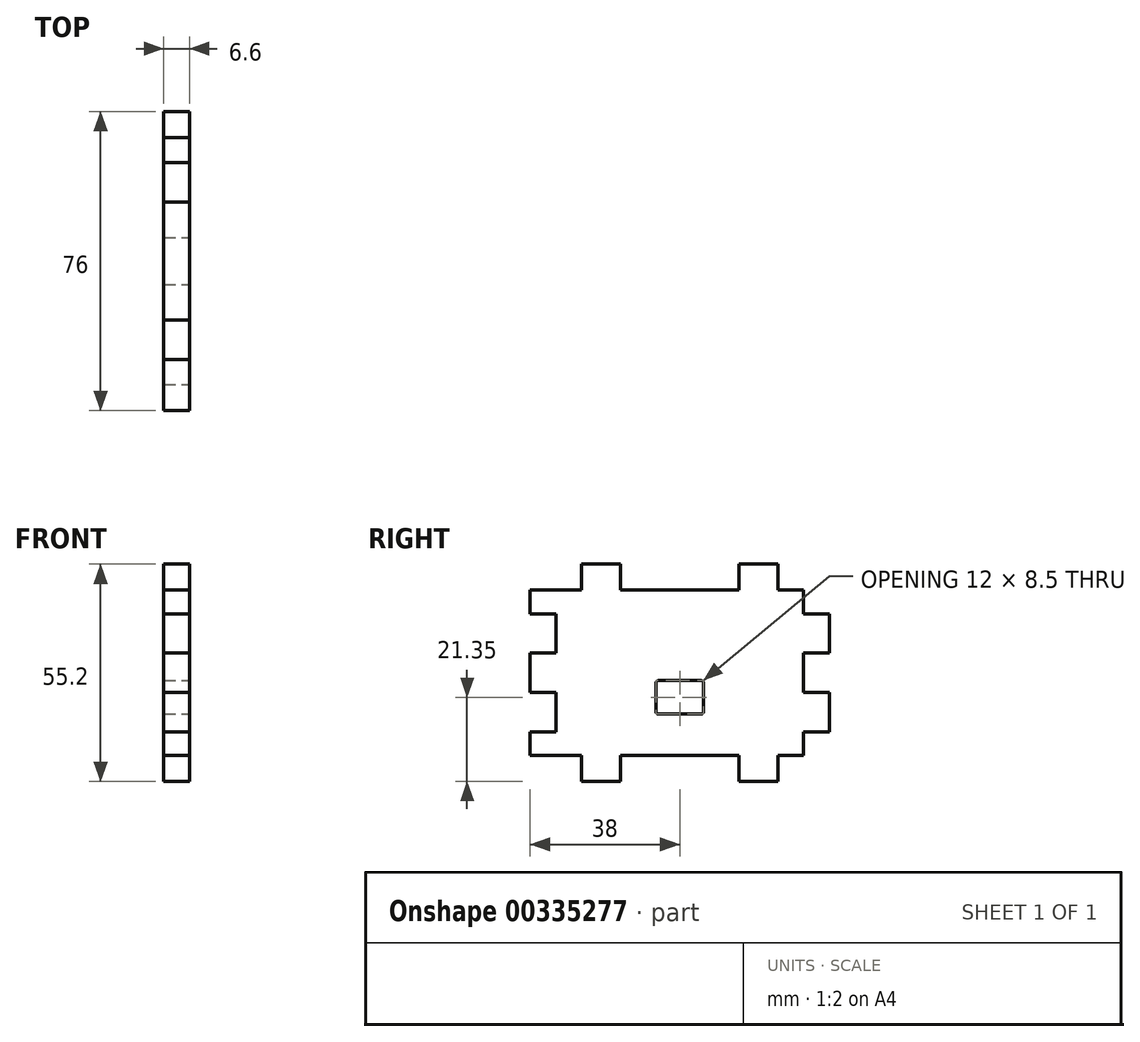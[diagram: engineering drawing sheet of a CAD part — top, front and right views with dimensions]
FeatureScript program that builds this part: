
annotation { "Feature Type Name" : "Feature", "Feature Type Description" : "" }
export const myFeature = defineFeature(function(context is Context, id is Id, definition is map)
    precondition{}
    {
        {
            var Q0;
            Q0=qCreatedBy(makeId("Right.planeOp"),FACE);
            var sketch = newSketch(context, id + "F0", { "sketchPlane" : qUnion([Q0])});
            skLineSegment(sketch, "E0.bottom", {"start": v(38, 21) * mm, "end": v(-38, 21) * mm});
            skLineSegment(sketch, "E0.top", {"start": v(38, -21) * mm, "end": v(-38, -21) * mm});
            skLineSegment(sketch, "E0.left", {"start": v(38, 21) * mm, "end": v(38, -21) * mm});
            skLineSegment(sketch, "E0.right", {"start": v(-38, 21) * mm, "end": v(-38, -21) * mm});
            skPoint(sketch, "E0.middle", {"position": v(0, 0) * mm});
            skSolve(sketch);
        }
        {
            var Q0;
            Q0=qSketchRegion(id+"F0",true);
            extrude(context, id + "F1", {"entities" : qUnion([Q0]), "depth" : 6.6 * mm});
        }
        {
            var Q0;
            Q0=makeQuery(id+"F1.opExtrude","CAP_FACE",FACE,{"disambiguationData":[OSD([sQuery(id+"F0.wireOp",EDGE,"E0.bottom"),sQuery(id+"F0.wireOp",EDGE,"E0.top"),sQuery(id+"F0.wireOp",EDGE,"E0.left"),sQuery(id+"F0.wireOp",EDGE,"E0.right")])],"isStart":false});
            var sketch = newSketch(context, id + "F2", { "sketchPlane" : qUnion([Q0])});
            skLineSegment(sketch, "E1", {"start": v(0, 21) * mm, "end": v(0, -21) * mm, "construction": true});
            skLineSegment(sketch, "E2", {"start": v(-38, 0) * mm, "end": v(38, 0) * mm, "construction": true});
            skLineSegment(sketch, "E3.bottom", {"start": v(-25, 27.6) * mm, "end": v(-15, 27.6) * mm});
            skLineSegment(sketch, "E3.top", {"start": v(-25, 21) * mm, "end": v(-15, 21) * mm});
            skLineSegment(sketch, "E3.left", {"start": v(-25, 27.6) * mm, "end": v(-25, 21) * mm});
            skLineSegment(sketch, "E3.right", {"start": v(-15, 27.6) * mm, "end": v(-15, 21) * mm});
            skLineSegment(sketch, "E4.MirrorCS", {"start": v(15, 27.6) * mm, "end": v(15, 21) * mm});
            skLineSegment(sketch, "E5.MirrorCS", {"start": v(25, 27.6) * mm, "end": v(25, 21) * mm});
            skLineSegment(sketch, "E6.MirrorCS", {"start": v(25, 21) * mm, "end": v(15, 21) * mm});
            skLineSegment(sketch, "E7.MirrorCS", {"start": v(25, 27.6) * mm, "end": v(15, 27.6) * mm});
            skLineSegment(sketch, "E8.MirrorCS", {"start": v(15, -27.6) * mm, "end": v(15, -21) * mm});
            skLineSegment(sketch, "E9.MirrorCS", {"start": v(-15, -27.6) * mm, "end": v(-15, -21) * mm});
            skLineSegment(sketch, "E10.MirrorCS", {"start": v(-25, -27.6) * mm, "end": v(-25, -21) * mm});
            skLineSegment(sketch, "E11.MirrorCS", {"start": v(-25, -21) * mm, "end": v(-15, -21) * mm});
            skLineSegment(sketch, "E12.MirrorCS", {"start": v(-25, -27.6) * mm, "end": v(-15, -27.6) * mm});
            skLineSegment(sketch, "E13.MirrorCS", {"start": v(25, -27.6) * mm, "end": v(25, -21) * mm});
            skLineSegment(sketch, "E14.MirrorCS", {"start": v(25, -21) * mm, "end": v(15, -21) * mm});
            skLineSegment(sketch, "E15.MirrorCS", {"start": v(25, -27.6) * mm, "end": v(15, -27.6) * mm});
            skSolve(sketch);
        }
        {
            var Q0;
            Q0 = qSketchRegion(id + "F2", true);
            extrude(context, id + "F3", {"entities" : qUnion([Q0]), "operationType" : NewBodyOperationType.ADD, "oppositeDirection" : true, "depth" : 6.6 * mm});
        }
        {
            var Q0;
            Q0=makeQuery(id+"F3.boolean.opBoolean","MERGE",FACE,{"derivedFrom":[makeQuery(id+"F1.opExtrude","CAP_FACE",FACE,{"disambiguationData":[OSD([sQuery(id+"F0.wireOp",EDGE,"E0.bottom"),sQuery(id+"F0.wireOp",EDGE,"E0.top"),sQuery(id+"F0.wireOp",EDGE,"E0.left"),sQuery(id+"F0.wireOp",EDGE,"E0.right")])],"isStart":false}),makeQuery(id+"F3.opExtrude","CAP_FACE",FACE,{"disambiguationData":[OSD([sQuery(id+"F2.wireOp",EDGE,"E3.bottom"),sQuery(id+"F2.wireOp",EDGE,"E3.top"),sQuery(id+"F2.wireOp",EDGE,"E3.left"),sQuery(id+"F2.wireOp",EDGE,"E3.right")])],"isStart":true}),makeQuery(id+"F3.opExtrude","CAP_FACE",FACE,{"disambiguationData":[OSD([sQuery(id+"F2.wireOp",EDGE,"E4.MirrorCS"),sQuery(id+"F2.wireOp",EDGE,"E5.MirrorCS"),sQuery(id+"F2.wireOp",EDGE,"E6.MirrorCS"),sQuery(id+"F2.wireOp",EDGE,"E7.MirrorCS")])],"isStart":true}),makeQuery(id+"F3.opExtrude","CAP_FACE",FACE,{"disambiguationData":[OSD([sQuery(id+"F2.wireOp",EDGE,"E8.MirrorCS"),sQuery(id+"F2.wireOp",EDGE,"E13.MirrorCS"),sQuery(id+"F2.wireOp",EDGE,"E14.MirrorCS"),sQuery(id+"F2.wireOp",EDGE,"E15.MirrorCS")])],"isStart":true}),makeQuery(id+"F3.opExtrude","CAP_FACE",FACE,{"disambiguationData":[OSD([sQuery(id+"F2.wireOp",EDGE,"E9.MirrorCS"),sQuery(id+"F2.wireOp",EDGE,"E10.MirrorCS"),sQuery(id+"F2.wireOp",EDGE,"E11.MirrorCS"),sQuery(id+"F2.wireOp",EDGE,"E12.MirrorCS")])],"isStart":true})]});
            var sketch = newSketch(context, id + "F4", { "sketchPlane" : qUnion([Q0])});
            skLineSegment(sketch, "E16", {"start": v(31.4, 21) * mm, "end": v(31.4, -21) * mm, "construction": true});
            skPoint(sketch, "E16.endSnap0", {"position": v(31.5, -21) * mm});
            skLineSegment(sketch, "E17.bottom", {"start": v(31.4, 21) * mm, "end": v(38, 21) * mm});
            skLineSegment(sketch, "E17.top", {"start": v(31.4, 15) * mm, "end": v(38, 15) * mm});
            skLineSegment(sketch, "E17.left", {"start": v(31.4, 21) * mm, "end": v(31.4, 15) * mm});
            skLineSegment(sketch, "E17.right", {"start": v(38, 21) * mm, "end": v(38, 15) * mm});
            skLineSegment(sketch, "E18", {"start": v(-38, 0) * mm, "end": v(38, 0) * mm, "construction": true});
            skLineSegment(sketch, "E19.MirrorCS", {"start": v(31.4, -15) * mm, "end": v(38, -15) * mm});
            skLineSegment(sketch, "E20.MirrorCS", {"start": v(31.4, -21) * mm, "end": v(31.4, -15) * mm});
            skLineSegment(sketch, "E21.MirrorCS", {"start": v(31.4, -21) * mm, "end": v(38, -21) * mm});
            skLineSegment(sketch, "E22.MirrorCS", {"start": v(38, -21) * mm, "end": v(38, -15) * mm});
            skLineSegment(sketch, "E23.bottom", {"start": v(31.4, 5) * mm, "end": v(38, 5) * mm});
            skLineSegment(sketch, "E23.top", {"start": v(31.4, -5) * mm, "end": v(38, -5) * mm});
            skLineSegment(sketch, "E23.left", {"start": v(31.4, 5) * mm, "end": v(31.4, -5) * mm});
            skLineSegment(sketch, "E23.right", {"start": v(38, 5) * mm, "end": v(38, -5) * mm});
            skPoint(sketch, "E23.middle", {"position": v(34.7, 0) * mm});
            skLineSegment(sketch, "E24", {"start": v(0, 21) * mm, "end": v(0, -21) * mm, "construction": true});
            skLineSegment(sketch, "E25.MirrorCS", {"start": v(-31.4, 21) * mm, "end": v(-31.4, -21) * mm, "construction": true});
            skLineSegment(sketch, "E26.bottom", {"start": v(-38, 15) * mm, "end": v(-31.4, 15) * mm});
            skLineSegment(sketch, "E26.top", {"start": v(-38, 5) * mm, "end": v(-31.4, 5) * mm});
            skLineSegment(sketch, "E26.left", {"start": v(-38, 15) * mm, "end": v(-38, 5) * mm});
            skLineSegment(sketch, "E26.right", {"start": v(-31.4, 15) * mm, "end": v(-31.4, 5) * mm});
            skLineSegment(sketch, "E27.MirrorCS", {"start": v(-38, -5) * mm, "end": v(-31.4, -5) * mm});
            skLineSegment(sketch, "E28.MirrorCS", {"start": v(-31.4, -15) * mm, "end": v(-31.4, -5) * mm});
            skLineSegment(sketch, "E29.MirrorCS", {"start": v(-38, -15) * mm, "end": v(-31.4, -15) * mm});
            skLineSegment(sketch, "E30.MirrorCS", {"start": v(-38, -15) * mm, "end": v(-38, -5) * mm});
            skSolve(sketch);
        }
        {
            var Q0;
            Q0 = qSketchRegion(id + "F4", true);
            extrude(context, id + "F5", {"entities" : qUnion([Q0]), "operationType" : NewBodyOperationType.REMOVE, "endBound" : BoundingType.UP_TO_NEXT, "oppositeDirection" : true, "depth" : 25 * mm});
        }
        {
            var Q0;
            Q0=makeQuery(id+"F3.boolean.opBoolean","MERGE",FACE,{"derivedFrom":[makeQuery(id+"F1.opExtrude","CAP_FACE",FACE,{"disambiguationData":[OSD([sQuery(id+"F0.wireOp",EDGE,"E0.bottom"),sQuery(id+"F0.wireOp",EDGE,"E0.top"),sQuery(id+"F0.wireOp",EDGE,"E0.left"),sQuery(id+"F0.wireOp",EDGE,"E0.right")])],"isStart":false}),makeQuery(id+"F3.opExtrude","CAP_FACE",FACE,{"disambiguationData":[OSD([sQuery(id+"F2.wireOp",EDGE,"E3.bottom"),sQuery(id+"F2.wireOp",EDGE,"E3.top"),sQuery(id+"F2.wireOp",EDGE,"E3.left"),sQuery(id+"F2.wireOp",EDGE,"E3.right")])],"isStart":true}),makeQuery(id+"F3.opExtrude","CAP_FACE",FACE,{"disambiguationData":[OSD([sQuery(id+"F2.wireOp",EDGE,"E4.MirrorCS"),sQuery(id+"F2.wireOp",EDGE,"E5.MirrorCS"),sQuery(id+"F2.wireOp",EDGE,"E6.MirrorCS"),sQuery(id+"F2.wireOp",EDGE,"E7.MirrorCS")])],"isStart":true}),makeQuery(id+"F3.opExtrude","CAP_FACE",FACE,{"disambiguationData":[OSD([sQuery(id+"F2.wireOp",EDGE,"E8.MirrorCS"),sQuery(id+"F2.wireOp",EDGE,"E13.MirrorCS"),sQuery(id+"F2.wireOp",EDGE,"E14.MirrorCS"),sQuery(id+"F2.wireOp",EDGE,"E15.MirrorCS")])],"isStart":true}),makeQuery(id+"F3.opExtrude","CAP_FACE",FACE,{"disambiguationData":[OSD([sQuery(id+"F2.wireOp",EDGE,"E9.MirrorCS"),sQuery(id+"F2.wireOp",EDGE,"E10.MirrorCS"),sQuery(id+"F2.wireOp",EDGE,"E11.MirrorCS"),sQuery(id+"F2.wireOp",EDGE,"E12.MirrorCS")])],"isStart":true})]});
            var sketch = newSketch(context, id + "F6", { "sketchPlane" : qUnion([Q0])});
            skLineSegment(sketch, "E31.bottom", {"start": v(6, -2) * mm, "end": v(-6, -2) * mm});
            skLineSegment(sketch, "E31.top", {"start": v(6, -10.5) * mm, "end": v(-6, -10.5) * mm});
            skLineSegment(sketch, "E31.left", {"start": v(6, -2) * mm, "end": v(6, -10.5) * mm});
            skLineSegment(sketch, "E31.right", {"start": v(-6, -2) * mm, "end": v(-6, -10.5) * mm});
            skPoint(sketch, "E31.middle", {"position": v(0, -6.25) * mm});
            skSolve(sketch);
        }
        {
            var Q0;
            Q0 = qSketchRegion(id + "F6", true);
            extrude(context, id + "F7", {"entities" : qUnion([Q0]), "operationType" : NewBodyOperationType.REMOVE, "endBound" : BoundingType.UP_TO_NEXT, "oppositeDirection" : true, "depth" : 25 * mm});
        }
        {
            var Q0;
            Q0=makeQuery(id+"F7.boolean.opBoolean","COPY",EDGE,{"derivedFrom":makeQuery(id+"F7.opExtrude","SWEPT_EDGE",EDGE,{"disambiguationData":[OSD([sQuery(id+"F6.wireOp",EDGE,"E31.bottom"),sQuery(id+"F6.wireOp",EDGE,"E31.right")])]})});
            var Q1;
            Q1=makeQuery(id+"F7.boolean.opBoolean","COPY",EDGE,{"derivedFrom":makeQuery(id+"F7.opExtrude","SWEPT_EDGE",EDGE,{"disambiguationData":[OSD([sQuery(id+"F6.wireOp",EDGE,"E31.bottom"),sQuery(id+"F6.wireOp",EDGE,"E31.left")])]})});
            var Q2;
            Q2=makeQuery(id+"F7.boolean.opBoolean","COPY",EDGE,{"derivedFrom":makeQuery(id+"F7.opExtrude","SWEPT_EDGE",EDGE,{"disambiguationData":[OSD([sQuery(id+"F6.wireOp",EDGE,"E31.top"),sQuery(id+"F6.wireOp",EDGE,"E31.left")])]})});
            var Q3;
            Q3=makeQuery(id+"F7.boolean.opBoolean","COPY",EDGE,{"derivedFrom":makeQuery(id+"F7.opExtrude","SWEPT_EDGE",EDGE,{"disambiguationData":[OSD([sQuery(id+"F6.wireOp",EDGE,"E31.top"),sQuery(id+"F6.wireOp",EDGE,"E31.right")])]})});
            fillet(context, id + "F8", {"entities" : qUnion([Q0, Q1, Q2, Q3]), "radius" : .5 * mm, "tangentPropagation" : true, "allowEdgeOverflow" : false});
        }
    });
